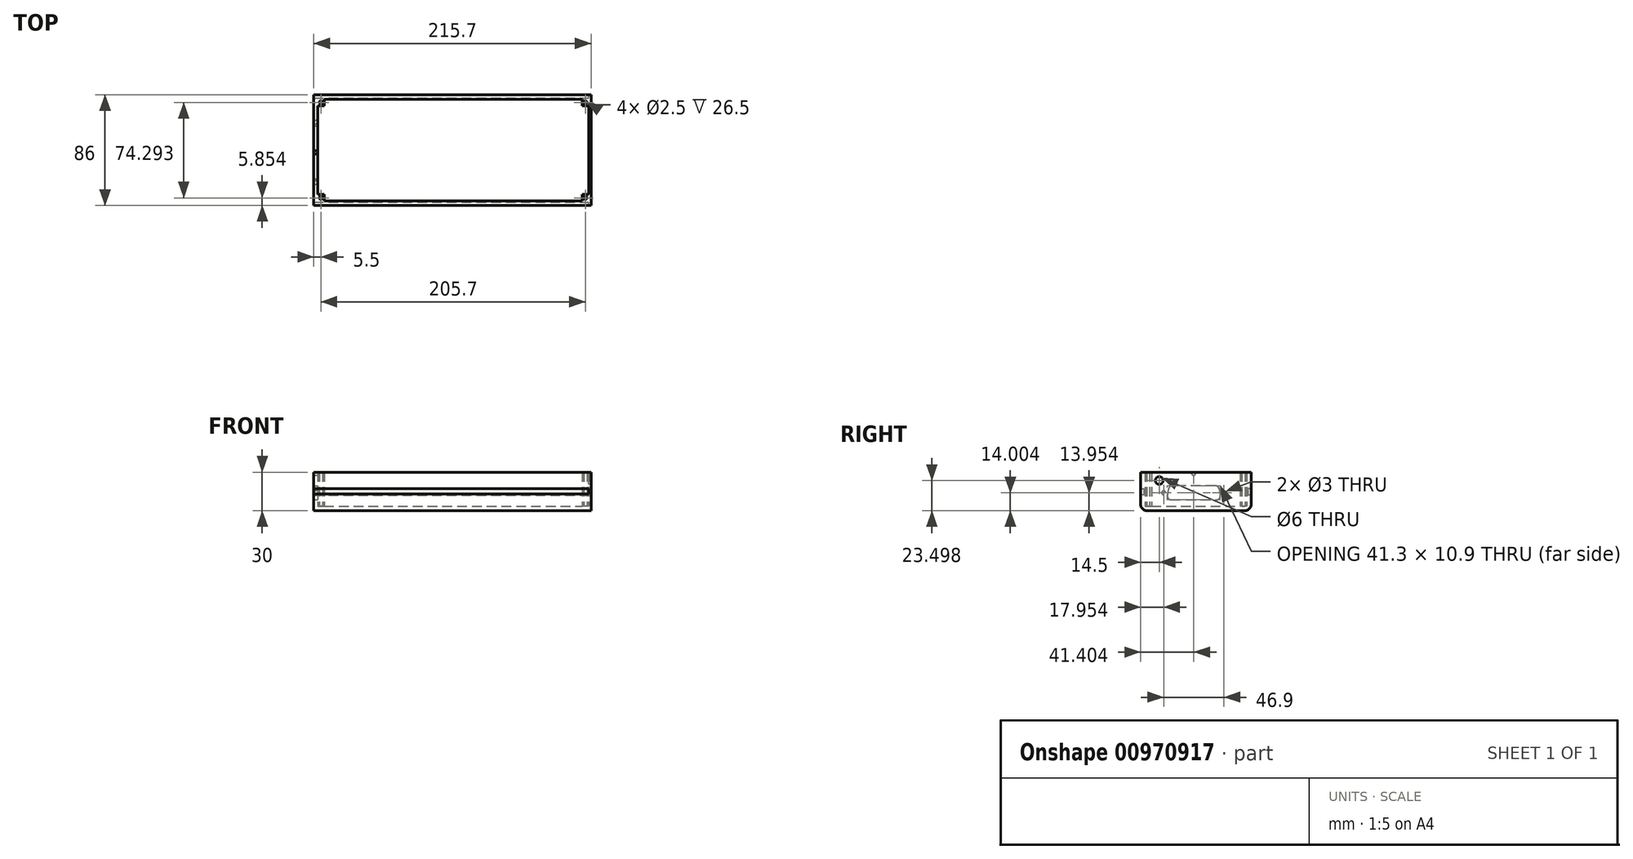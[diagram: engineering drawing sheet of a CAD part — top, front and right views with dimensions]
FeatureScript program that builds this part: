
annotation { "Feature Type Name" : "Feature", "Feature Type Description" : "" }
export const myFeature = defineFeature(function(context is Context, id is Id, definition is map)
    precondition{}
    {
        {
            var Q0;
            Q0=qCreatedBy(makeId("Right.planeOp"),FACE);
            var sketch = newSketch(context, id + "F0", { "sketchPlane" : qUnion([Q0])});
            skLineSegment(sketch, "E0", {"start": v(-79, -3.23) * mm, "end": v(-82.5, -3.23) * mm});
            skLineSegment(sketch, "E1", {"start": v(-82.5, -3.23) * mm, "end": v(-82.5, -16.23) * mm});
            skLineSegment(sketch, "E2", {"start": v(-82.5, -16.23) * mm, "end": v(-80, -16.23) * mm});
            skLineSegment(sketch, "E3", {"start": v(-80, -16.23) * mm, "end": v(-80, -21.23) * mm});
            skLineSegment(sketch, "E4", {"start": v(-80, -21.23) * mm, "end": v(-82.5, -20.23) * mm});
            skLineSegment(sketch, "E5", {"start": v(-82.5, -20.23) * mm, "end": v(-82.5, -28.23) * mm});
            skLineSegment(sketch, "E6", {"start": v(-77.5, -33.23) * mm, "end": v(-1.5, -33.23) * mm});
            skLineSegment(sketch, "E7", {"start": v(-79, -29.73) * mm, "end": v(-79, -3.23) * mm});
            skLineSegment(sketch, "E8", {"start": v(-79, -29.73) * mm, "end": v(0, -29.73) * mm});
            skLineSegment(sketch, "E9", {"start": v(3.5, -3.23) * mm, "end": v(0, -3.23) * mm});
            skPoint(sketch, "E10.visualSharp", {"position": v(-82.5, -33.23) * mm});
            skArc(sketch, "E10.filletArc", {"start": v(-82.5, -28.23) * mm, "mid": v(-81.04, -31.77) * mm, "end": v(-77.5, -33.23) * mm});
            skLineSegment(sketch, "E11", {"start": v(3.5, -3.23) * mm, "end": v(3.5, -16.23) * mm});
            skLineSegment(sketch, "E12", {"start": v(3.5, -28.23) * mm, "end": v(3.5, -20.23) * mm});
            skLineSegment(sketch, "E13", {"start": v(0, -3.23) * mm, "end": v(0, -29.73) * mm});
            skLineSegment(sketch, "E14", {"start": v(3.5, -16.23) * mm, "end": v(1, -16.23) * mm});
            skLineSegment(sketch, "E15", {"start": v(1, -16.23) * mm, "end": v(1, -21.23) * mm});
            skLineSegment(sketch, "E16", {"start": v(1, -21.23) * mm, "end": v(3.5, -20.23) * mm});
            skLineSegment(sketch, "E17", {"start": v(-79, -3.23) * mm, "end": v(0, -3.23) * mm});
            skLineSegment(sketch, "E18", {"start": v(-82.5, -16.23) * mm, "end": v(-82.5, -20.23) * mm});
            skLineSegment(sketch, "E19", {"start": v(3.5, -16.23) * mm, "end": v(3.5, -20.23) * mm});
            skPoint(sketch, "E20.visualSharp", {"position": v(3.5, -33.23) * mm});
            skArc(sketch, "E20.filletArc", {"start": v(-1.5, -33.23) * mm, "mid": v(2.04, -31.77) * mm, "end": v(3.5, -28.23) * mm});
            skCircle(sketch, "E21", {"center": v(-68, -9.73) * mm, "radius": 3 * mm});
            skSolve(sketch);
        }
        {
            var Q0;
            Q0=makeQuery(id+"F0.imprint","IMPRINT",FACE,{"disambiguationData":[TD([[makeQuery(id+"F0.imprint","IMPRINT",EDGE,{"derivedFrom":sQuery(id+"F0.wireOp",EDGE,"E0")}),1.0]])]});
            extrude(context, id + "F1", {"entities" : qUnion([Q0]), "oppositeDirection" : true, "depth" : 210.7 * mm, "offsetDistance" : 25 * mm});
        }
        {
            var Q0;
            Q0=makeQuery(id+"F0.imprint","IMPRINT",FACE,{"disambiguationData":[TD([[makeQuery(id+"F0.imprint","IMPRINT",EDGE,{"derivedFrom":sQuery(id+"F0.wireOp",EDGE,"E7")}),-1.0]])]});
            var Q1;
            Q1=makeQuery(id+"F0.imprint","IMPRINT",FACE,{"disambiguationData":[TD([[makeQuery(id+"F0.imprint","IMPRINT",EDGE,{"derivedFrom":sQuery(id+"F0.wireOp",EDGE,"E2")}),-1.0]])]});
            var Q2;
            Q2=makeQuery(id+"F0.imprint","IMPRINT",FACE,{"disambiguationData":[TD([[makeQuery(id+"F0.imprint","IMPRINT",EDGE,{"derivedFrom":sQuery(id+"F0.wireOp",EDGE,"E14")}),1.0]])]});
            extrude(context, id + "F2", {"entities" : qUnion([Q0, Q1, Q2]), "operationType" : NewBodyOperationType.ADD, "depth" : 2 * mm, "offsetDistance" : 25 * mm});
        }
        {
            var Q0;
            Q0=makeQuery(id+"F0.imprint","IMPRINT",FACE,{"disambiguationData":[TD([[makeQuery(id+"F0.imprint","IMPRINT",EDGE,{"derivedFrom":sQuery(id+"F0.wireOp",EDGE,"E0")}),1.0]])]});
            var Q1;
            Q1=makeQuery(id+"F2.opExtrude","CAP_FACE",FACE,{"disambiguationData":[OSD([sQuery(id+"F0.wireOp",EDGE,"E7"),sQuery(id+"F0.wireOp",EDGE,"E8"),sQuery(id+"F0.wireOp",EDGE,"E13"),sQuery(id+"F0.wireOp",EDGE,"E17")])],"isStart":false});
            extrude(context, id + "F3", {"entities" : qUnion([Q0]), "operationType" : NewBodyOperationType.ADD, "endBound" : BoundingType.UP_TO_SURFACE, "depth" : 25 * mm, "endBoundEntityFace" : qUnion([Q1]), "offsetDistance" : 25 * mm});
        }
        {
            var Q0;
            Q0=makeQuery(id+"F1.opExtrude","CAP_FACE",FACE,{"disambiguationData":[OSD([sQuery(id+"F0.wireOp",EDGE,"E0"),sQuery(id+"F0.wireOp",EDGE,"E1"),sQuery(id+"F0.wireOp",EDGE,"E2"),sQuery(id+"F0.wireOp",EDGE,"E3"),sQuery(id+"F0.wireOp",EDGE,"E4"),sQuery(id+"F0.wireOp",EDGE,"E5"),sQuery(id+"F0.wireOp",EDGE,"E6"),sQuery(id+"F0.wireOp",EDGE,"E7"),sQuery(id+"F0.wireOp",EDGE,"E8"),sQuery(id+"F0.wireOp",EDGE,"E9"),sQuery(id+"F0.wireOp",EDGE,"E10.filletArc"),sQuery(id+"F0.wireOp",EDGE,"E11"),sQuery(id+"F0.wireOp",EDGE,"E12"),sQuery(id+"F0.wireOp",EDGE,"E13"),sQuery(id+"F0.wireOp",EDGE,"E14"),sQuery(id+"F0.wireOp",EDGE,"E15"),sQuery(id+"F0.wireOp",EDGE,"E16"),sQuery(id+"F0.wireOp",EDGE,"E20.filletArc")])],"isStart":false});
            var sketch = newSketch(context, id + "F4", { "sketchPlane" : qUnion([Q0])});
            skLineSegment(sketch, "E22", {"start": v(-3.5, -3.23) * mm, "end": v(82.5, -3.23) * mm});
            skLineSegment(sketch, "E23", {"start": v(82.5, -3.23) * mm, "end": v(82.5, -28.23) * mm});
            skLineSegment(sketch, "E24", {"start": v(-3.5, -3.23) * mm, "end": v(-3.5, -28.23) * mm});
            skLineSegment(sketch, "E25", {"start": v(1.5, -33.23) * mm, "end": v(77.5, -33.23) * mm});
            skPoint(sketch, "E26.visualSharp", {"position": v(-3.5, -33.23) * mm});
            skArc(sketch, "E26.filletArc", {"start": v(-3.5, -28.23) * mm, "mid": v(-2.04, -31.77) * mm, "end": v(1.5, -33.23) * mm});
            skPoint(sketch, "E27.newPointA", {"position": v(82.5, -28.23) * mm});
            skPoint(sketch, "E27.newPointB", {"position": v(82.5, -33.23) * mm});
            skArc(sketch, "E27.filletArc", {"start": v(77.5, -33.23) * mm, "mid": v(81.04, -31.77) * mm, "end": v(82.5, -28.23) * mm});
            skLineSegment(sketch, "E28", {"start": v(14.65, -25.48) * mm, "end": v(67.55, -25.48) * mm});
            skLineSegment(sketch, "E29", {"start": v(67.55, -25.48) * mm, "end": v(67.55, -13.08) * mm});
            skLineSegment(sketch, "E30", {"start": v(67.55, -13.08) * mm, "end": v(14.65, -13.08) * mm});
            skCircle(sketch, "E31", {"center": v(17.65, -19.28) * mm, "radius": 1.5 * mm});
            skLineSegment(sketch, "E32", {"start": v(41.1, -25.48) * mm, "end": v(41.1, -13.08) * mm, "construction": true});
            skCircle(sketch, "E33.MirrorC", {"center": v(64.55, -19.28) * mm, "radius": 1.5 * mm});
            skLineSegment(sketch, "E34", {"start": v(21.45, -16.2) * mm, "end": v(20.5, -21.1) * mm});
            skLineSegment(sketch, "E35.MirrorCS", {"start": v(60.75, -16.2) * mm, "end": v(61.7, -21.1) * mm});
            skLineSegment(sketch, "E36", {"start": v(24.4, -13.78) * mm, "end": v(57.8, -13.78) * mm});
            skLineSegment(sketch, "E37", {"start": v(58.75, -24.68) * mm, "end": v(23.45, -24.68) * mm});
            skPoint(sketch, "E38.visualSharp", {"position": v(21.91, -13.78) * mm});
            skArc(sketch, "E38.filletArc", {"start": v(24.4, -13.78) * mm, "mid": v(22.48, -14.46) * mm, "end": v(21.45, -16.2) * mm});
            skPoint(sketch, "E39.visualSharp", {"position": v(19.81, -24.68) * mm});
            skArc(sketch, "E39.filletArc", {"start": v(20.5, -21.1) * mm, "mid": v(21.13, -23.59) * mm, "end": v(23.45, -24.68) * mm});
            skPoint(sketch, "E40.visualSharp", {"position": v(60.28, -13.78) * mm});
            skArc(sketch, "E40.filletArc", {"start": v(60.75, -16.2) * mm, "mid": v(59.7, -14.46) * mm, "end": v(57.8, -13.78) * mm});
            skPoint(sketch, "E41.visualSharp", {"position": v(62.38, -24.68) * mm});
            skArc(sketch, "E41.filletArc", {"start": v(58.75, -24.68) * mm, "mid": v(61.06, -23.59) * mm, "end": v(61.7, -21.1) * mm});
            skCircle(sketch, "E42", {"center": v(41.25, -4.08) * mm, "radius": 1.6 * mm});
            skSolve(sketch);
        }
        {
            var Q0;
            {var subQ1=makeQuery(id+"F1.opExtrude","CAP_EDGE",EDGE,{"disambiguationData":[OSD([sQuery(id+"F0.wireOp",EDGE,"E7")])],"isStart":false});Q0=makeQuery(id+"F4.imprint","IMPRINT",FACE,{"disambiguationData":[TD([[makeQuery(id+"F4.imprint","IMPRINT",EDGE,{"derivedFrom":subQ1}),1.0]])]});}
            var Q1;
            Q1=makeQuery(id+"F4.imprint","IMPRINT",FACE,{"disambiguationData":[TD([[makeQuery(id+"F4.imprint","IMPRINT",EDGE,{"derivedFrom":sQuery(id+"F4.wireOp",EDGE,"E25")}),-1.0]])]});
            extrude(context, id + "F5", {"entities" : qUnion([Q0, Q1]), "operationType" : NewBodyOperationType.ADD, "depth" : 3 * mm, "offsetDistance" : 25 * mm});
        }
        {
            var Q0;
            Q0=makeQuery(id+"F1.opExtrude","SWEPT_FACE",FACE,{"disambiguationData":[OSD([sQuery(id+"F0.wireOp",EDGE,"E8")])]});
            var sketch = newSketch(context, id + "F6", { "sketchPlane" : qUnion([Q0])});
            skLineSegment(sketch, "E43.bottom", {"start": v(-210.7, 0) * mm, "end": v(-205.7, 0) * mm});
            skLineSegment(sketch, "E43.top", {"start": v(-210.7, -5) * mm, "end": v(-205.7, -5) * mm});
            skLineSegment(sketch, "E43.left", {"start": v(-210.7, 0) * mm, "end": v(-210.7, -5) * mm});
            skLineSegment(sketch, "E43.right", {"start": v(-205.7, 0) * mm, "end": v(-205.7, -5) * mm});
            skLineSegment(sketch, "E44", {"start": v(10.88, -39.5) * mm, "end": v(-244.63, -39.5) * mm, "construction": true});
            skPoint(sketch, "E44.startSnap0", {"position": v(-210.7, -39.5) * mm});
            skLineSegment(sketch, "E45.MirrorCS", {"start": v(-210.7, -74) * mm, "end": v(-205.7, -74) * mm});
            skLineSegment(sketch, "E46.MirrorCS", {"start": v(-205.7, -79) * mm, "end": v(-205.7, -74) * mm});
            skLineSegment(sketch, "E47.MirrorCS", {"start": v(-210.7, -79) * mm, "end": v(-210.7, -74) * mm});
            skLineSegment(sketch, "E48", {"start": v(-105.35, -79) * mm, "end": v(-105.35, 15.53) * mm, "construction": true});
            skLineSegment(sketch, "E49.MirrorCS", {"start": v(0, -5) * mm, "end": v(-5, -5) * mm});
            skLineSegment(sketch, "E50.MirrorCS", {"start": v(-5, 0) * mm, "end": v(-5, -5) * mm});
            skLineSegment(sketch, "E51.MirrorCS", {"start": v(0, 0) * mm, "end": v(-5, 0) * mm});
            skPoint(sketch, "E52", {"position": v(0, -39.5) * mm});
            skLineSegment(sketch, "E53.MirrorCS", {"start": v(0, -79) * mm, "end": v(-5, -79) * mm});
            skLineSegment(sketch, "E54.MirrorCS", {"start": v(-5, -79) * mm, "end": v(-5, -74) * mm});
            skLineSegment(sketch, "E55", {"start": v(0, -5) * mm, "end": v(0, 0) * mm});
            skLineSegment(sketch, "E56.MirrorCS", {"start": v(0, -74) * mm, "end": v(0, -79) * mm});
            skLineSegment(sketch, "E57.MirrorCS", {"start": v(0, -74) * mm, "end": v(-5, -74) * mm});
            skCircle(sketch, "E58", {"center": v(-2.5, -2.35) * mm, "radius": 1.25 * mm});
            skPoint(sketch, "E58.centerSnap0", {"position": v(-2.5, -5) * mm});
            skCircle(sketch, "E59.MirrorC", {"center": v(-2.5, -76.65) * mm, "radius": 1.25 * mm});
            skCircle(sketch, "E60.MirrorC", {"center": v(-208.2, -76.65) * mm, "radius": 1.25 * mm});
            skCircle(sketch, "E61.MirrorC", {"center": v(-208.2, -2.35) * mm, "radius": 1.25 * mm});
            skSolve(sketch);
        }
        {
            var Q0;
            Q0=makeQuery(id+"F6.imprint","IMPRINT",FACE,{"disambiguationData":[TD([[makeQuery(id+"F6.imprint","IMPRINT",EDGE,{"derivedFrom":sQuery(id+"F6.wireOp",EDGE,"E54.MirrorCS")}),-1.0]])]});
            var Q1;
            Q1=makeQuery(id+"F6.imprint","IMPRINT",FACE,{"disambiguationData":[TD([[makeQuery(id+"F6.imprint","IMPRINT",EDGE,{"derivedFrom":sQuery(id+"F6.wireOp",EDGE,"E49.MirrorCS")}),-1.0]])]});
            var Q2;
            Q2=makeQuery(id+"F6.imprint","IMPRINT",FACE,{"disambiguationData":[TD([[makeQuery(id+"F6.imprint","IMPRINT",EDGE,{"derivedFrom":sQuery(id+"F6.wireOp",EDGE,"E43.bottom")}),-1.0]])]});
            var Q3;
            Q3=makeQuery(id+"F6.imprint","IMPRINT",FACE,{"disambiguationData":[TD([[makeQuery(id+"F6.imprint","IMPRINT",EDGE,{"derivedFrom":sQuery(id+"F6.wireOp",EDGE,"E45.MirrorCS")}),-1.0]])]});
            var Q4;
            {var subQ0=sQuery(id+"F0.wireOp",EDGE,"E9");var subQ1=sQuery(id+"F0.wireOp",EDGE,"E0");Q4=makeQuery(id+"F5.boolean.opBoolean","MERGE",FACE,{"derivedFrom":[makeQuery(id+"F3.boolean.opBoolean","MERGE",FACE,{"derivedFrom":[makeQuery(id+"F1.opExtrude","SWEPT_FACE",FACE,{"disambiguationData":[OSD([subQ1])]}),makeQuery(id+"F1.opExtrude","SWEPT_FACE",FACE,{"disambiguationData":[OSD([subQ0])]}),makeQuery(id+"F2.opExtrude","SWEPT_FACE",FACE,{"disambiguationData":[OSD([sQuery(id+"F0.wireOp",EDGE,"E17")])]}),makeQuery(id+"F3.opExtrude","SWEPT_FACE",FACE,{"disambiguationData":[OSD([subQ1])]}),makeQuery(id+"F3.opExtrude","SWEPT_FACE",FACE,{"disambiguationData":[OSD([subQ0])]})]}),makeQuery(id+"F5.opExtrude","SWEPT_FACE",FACE,{"disambiguationData":[OSD([sQuery(id+"F4.wireOp",EDGE,"E22")])]})]});}
            extrude(context, id + "F7", {"entities" : qUnion([Q0, Q1, Q2, Q3]), "operationType" : NewBodyOperationType.ADD, "endBound" : BoundingType.UP_TO_SURFACE, "depth" : 25 * mm, "endBoundEntityFace" : qUnion([Q4]), "offsetDistance" : 25 * mm});
        }
    });
